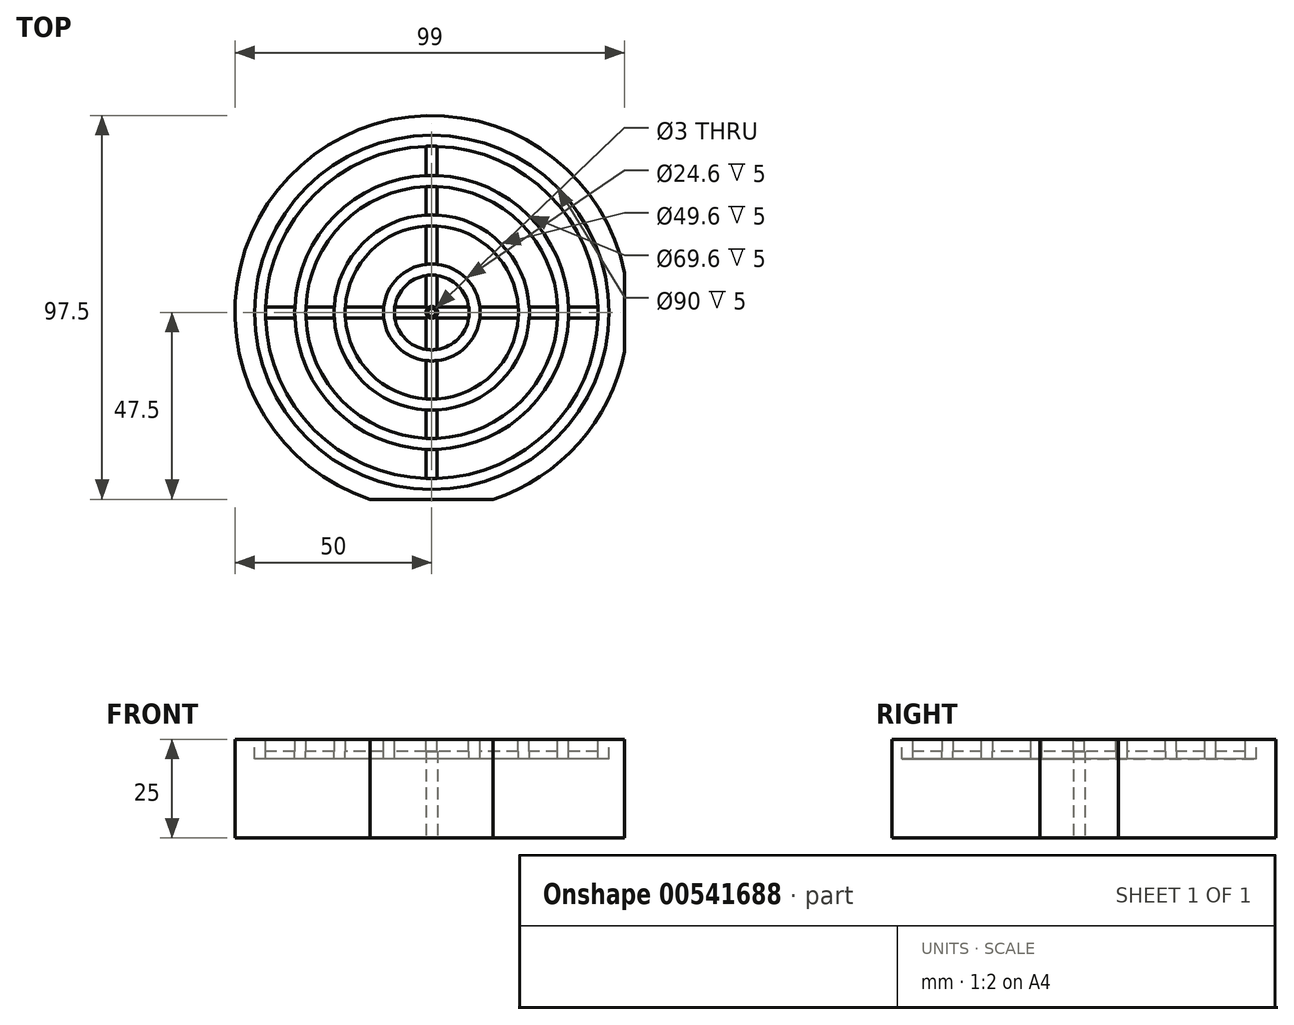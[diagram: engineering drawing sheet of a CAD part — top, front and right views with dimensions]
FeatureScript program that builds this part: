
annotation { "Feature Type Name" : "Feature", "Feature Type Description" : "" }
export const myFeature = defineFeature(function(context is Context, id is Id, definition is map)
    precondition{}
    {
        {
            var Q0;
            Q0=qCreatedBy(makeId("Top.planeOp"),FACE);
            var sketch = newSketch(context, id + "F0", { "sketchPlane" : qUnion([Q0])});
            skCircle(sketch, "E0", {"center": v(0, 0) * mm, "radius": 50 * mm});
            skCircle(sketch, "E1", {"center": v(0, 0) * mm, "radius": 1.5 * mm});
            skSolve(sketch);
        }
        {
            var Q0;
            Q0=qSketchRegion(id+"F0",true);
            extrude(context, id + "F1", {"entities" : qUnion([Q0]), "depth" : 25 * mm, "offsetDistance" : 25 * mm});
        }
        {
            var Q0;
            Q0=makeQuery(id+"F1.opExtrude","CAP_FACE",FACE,{"disambiguationData":[OSD([sQuery(id+"F0.wireOp",EDGE,"E0")])],"isStart":false});
            var sketch = newSketch(context, id + "F2", { "sketchPlane" : qUnion([Q0])});
            skCircle(sketch, "E2", {"center": v(0, 0) * mm, "radius": 45 * mm});
            skCircle(sketch, "E3.0", {"center": v(0, 0) * mm, "radius": 42.22 * mm});
            skCircle(sketch, "E4", {"center": v(0, 0) * mm, "radius": 32.5 * mm});
            skCircle(sketch, "E5.0", {"center": v(0, 0) * mm, "radius": 29.72 * mm});
            skCircle(sketch, "E6", {"center": v(0, 0) * mm, "radius": 22.5 * mm});
            skCircle(sketch, "E7", {"center": v(0, 0) * mm, "radius": 10 * mm});
            skCircle(sketch, "E8.0", {"center": v(0, 0) * mm, "radius": 7.22 * mm});
            skCircle(sketch, "E9.0", {"center": v(0, 0) * mm, "radius": 19.72 * mm});
            skLineSegment(sketch, "E10", {"start": v(-1, 44.99) * mm, "end": v(-1, 7.15) * mm});
            skLineSegment(sketch, "E11", {"start": v(1.39, 44.98) * mm, "end": v(1.4, -7.08) * mm});
            skLineSegment(sketch, "E12", {"start": v(0, 7.22) * mm, "end": v(0, 45) * mm, "construction": true});
            skLineSegment(sketch, "E13.1.0", {"start": v(-32.32, 31.02) * mm, "end": v(-5.57, 4.27) * mm});
            skLineSegment(sketch, "E13.1.1", {"start": v(-30.63, 32.7) * mm, "end": v(6.19, -4.1) * mm});
            skLineSegment(sketch, "E13.2.0", {"start": v(-44.6, -1) * mm, "end": v(-6.76, -1) * mm});
            skLineSegment(sketch, "E13.2.1", {"start": v(-44.59, 1.39) * mm, "end": v(7.47, 1.4) * mm});
            skPoint(sketch, "E13.center", {"position": v(0.2, 0.2) * mm});
            skLineSegment(sketch, "E14.2.3.0", {"start": v(-30.63, -32.32) * mm, "end": v(-3.88, -5.57) * mm});
            skLineSegment(sketch, "E14.3.3.0", {"start": v(-32.32, -30.63) * mm, "end": v(4.5, 6.19) * mm});
            skLineSegment(sketch, "E15.2.4.0", {"start": v(1.4, -44.6) * mm, "end": v(1.39, -6.76) * mm});
            skLineSegment(sketch, "E15.3.4.0", {"start": v(-1, -44.59) * mm, "end": v(-1, 7.47) * mm});
            skLineSegment(sketch, "E15.2.5.0", {"start": v(32.71, -30.63) * mm, "end": v(5.96, -3.88) * mm});
            skLineSegment(sketch, "E15.3.5.0", {"start": v(31.02, -32.32) * mm, "end": v(-5.8, 4.5) * mm});
            skLineSegment(sketch, "E15.2.6.0", {"start": v(44.99, 1.4) * mm, "end": v(7.15, 1.4) * mm});
            skLineSegment(sketch, "E15.3.6.0", {"start": v(44.98, -1) * mm, "end": v(-7.08, -1) * mm});
            skLineSegment(sketch, "E15.2.7.0", {"start": v(31.02, 32.71) * mm, "end": v(4.27, 5.96) * mm});
            skLineSegment(sketch, "E15.3.7.0", {"start": v(32.7, 31.02) * mm, "end": v(-4.1, -5.8) * mm});
            skLineSegment(sketch, "E16", {"start": v(7.15, 1.4) * mm, "end": v(7.47, 1.4) * mm});
            skLineSegment(sketch, "E17", {"start": v(-7.08, -1) * mm, "end": v(-6.76, -1) * mm});
            skLineSegment(sketch, "E18", {"start": v(1.4, -6.76) * mm, "end": v(1.4, -7.08) * mm});
            skLineSegment(sketch, "E19", {"start": v(-1, 7.47) * mm, "end": v(-1, 7.15) * mm});
            skSolve(sketch);
        }
        {
            var Q0;
            Q0=qSketchRegion(id+"F2",true);
            extrude(context, id + "F3", {"entities" : qUnion([Q0]), "operationType" : NewBodyOperationType.REMOVE, "oppositeDirection" : true, "depth" : 5 * mm, "offsetDistance" : 25 * mm});
        }
        {
            var Q0;
            {var subQ0=sQuery(id+"F0.wireOp",EDGE,"E1");Q0=makeQuery(id+"F3.boolean.opBoolean","SPLIT",FACE,{"disambiguationData":[TD([makeQuery(id+"F1.opExtrude","SWEPT_FACE",FACE,{"disambiguationData":[OSD([subQ0])]})])],"derivedFrom":makeQuery(id+"F1.opExtrude","CAP_FACE",FACE,{"disambiguationData":[OSD([sQuery(id+"F0.wireOp",EDGE,"E0"),subQ0])],"isStart":false})});}
            var sketch = newSketch(context, id + "F4", { "sketchPlane" : qUnion([Q0])});
            skCircle(sketch, "E20", {"center": v(0, 0) * mm, "radius": 9.5 * mm});
            skCircle(sketch, "E21", {"center": v(0, 0) * mm, "radius": 12.3 * mm});
            skSolve(sketch);
        }
        {
            var Q0;
            Q0=makeQuery(id+"F4.imprint","IMPRINT",FACE,{"disambiguationData":[TD([[makeQuery(id+"F4.imprint","IMPRINT",EDGE,{"derivedFrom":sQuery(id+"F4.wireOp",EDGE,"E20")}),-1.0]])]});
            extrude(context, id + "F5", {"entities" : qUnion([Q0]), "operationType" : NewBodyOperationType.REMOVE, "oppositeDirection" : true, "depth" : 5 * mm, "offsetDistance" : 25 * mm});
        }
        {
            var Q0;
            {var subQ0=makeQuery(id+"F3.opExtrude","SWEPT_FACE",FACE,{"disambiguationData":[OSD([sQuery(id+"F2.wireOp",EDGE,"E3.0")])]});var subQ1=sQuery(id+"F0.wireOp",EDGE,"E1");Q0=makeQuery(id+"F5.boolean.opBoolean","SPLIT",FACE,{"disambiguationData":[TD([makeQuery(id+"F3.boolean.opBoolean","COPY",FACE,{"derivedFrom":subQ0})])],"derivedFrom":makeQuery(id+"F3.boolean.opBoolean","SPLIT",FACE,{"disambiguationData":[TD([makeQuery(id+"F1.opExtrude","SWEPT_FACE",FACE,{"disambiguationData":[OSD([subQ1])]})])],"derivedFrom":makeQuery(id+"F1.opExtrude","CAP_FACE",FACE,{"disambiguationData":[OSD([sQuery(id+"F0.wireOp",EDGE,"E0"),subQ1])],"isStart":false})})});}
            var sketch = newSketch(context, id + "F6", { "sketchPlane" : qUnion([Q0])});
            skCircle(sketch, "E22", {"center": v(0, 0) * mm, "radius": 22 * mm});
            skCircle(sketch, "E23", {"center": v(0, 0) * mm, "radius": 24.8 * mm});
            skSolve(sketch);
        }
        {
            var Q0;
            Q0=makeQuery(id+"F6.imprint","IMPRINT",FACE,{"disambiguationData":[TD([[makeQuery(id+"F6.imprint","IMPRINT",EDGE,{"derivedFrom":sQuery(id+"F6.wireOp",EDGE,"E22")}),-1.0]])]});
            extrude(context, id + "F7", {"entities" : qUnion([Q0]), "operationType" : NewBodyOperationType.REMOVE, "oppositeDirection" : true, "depth" : 5 * mm, "offsetDistance" : 25 * mm});
        }
        {
            var Q0;
            {var subQ0=makeQuery(id+"F3.opExtrude","SWEPT_FACE",FACE,{"disambiguationData":[OSD([sQuery(id+"F2.wireOp",EDGE,"E3.0")])]});var subQ1=makeQuery(id+"F3.boolean.opBoolean","COPY",FACE,{"derivedFrom":subQ0});var subQ2=sQuery(id+"F0.wireOp",EDGE,"E1");Q0=makeQuery(id+"F7.boolean.opBoolean","SPLIT",FACE,{"disambiguationData":[TD([subQ1])],"derivedFrom":makeQuery(id+"F5.boolean.opBoolean","SPLIT",FACE,{"disambiguationData":[TD([subQ1])],"derivedFrom":makeQuery(id+"F3.boolean.opBoolean","SPLIT",FACE,{"disambiguationData":[TD([makeQuery(id+"F1.opExtrude","SWEPT_FACE",FACE,{"disambiguationData":[OSD([subQ2])]})])],"derivedFrom":makeQuery(id+"F1.opExtrude","CAP_FACE",FACE,{"disambiguationData":[OSD([sQuery(id+"F0.wireOp",EDGE,"E0"),subQ2])],"isStart":false})})})});}
            var sketch = newSketch(context, id + "F8", { "sketchPlane" : qUnion([Q0])});
            skCircle(sketch, "E24", {"center": v(0, 0) * mm, "radius": 32 * mm});
            skCircle(sketch, "E25", {"center": v(0, 0) * mm, "radius": 34.8 * mm});
            skSolve(sketch);
        }
        {
            var Q0;
            Q0=makeQuery(id+"F8.imprint","IMPRINT",FACE,{"disambiguationData":[TD([[makeQuery(id+"F8.imprint","IMPRINT",EDGE,{"derivedFrom":sQuery(id+"F8.wireOp",EDGE,"E24")}),-1.0]])]});
            extrude(context, id + "F9", {"entities" : qUnion([Q0]), "operationType" : NewBodyOperationType.REMOVE, "oppositeDirection" : true, "depth" : 5 * mm, "offsetDistance" : 25 * mm});
        }
        {
            var Q0;
            {var subQ0=sQuery(id+"F0.wireOp",EDGE,"E0");Q0=makeQuery(id+"F3.boolean.opBoolean","SPLIT",FACE,{"disambiguationData":[TD([makeQuery(id+"F1.opExtrude","SWEPT_FACE",FACE,{"disambiguationData":[OSD([subQ0])]})])],"derivedFrom":makeQuery(id+"F1.opExtrude","CAP_FACE",FACE,{"disambiguationData":[OSD([subQ0,sQuery(id+"F0.wireOp",EDGE,"E1")])],"isStart":false})});}
            var sketch = newSketch(context, id + "F10", { "sketchPlane" : qUnion([Q0])});
            skLineSegment(sketch, "E26.bottom", {"start": v(1.4, 44) * mm, "end": v(-1.4, 44) * mm});
            skLineSegment(sketch, "E26.top", {"start": v(1.4, -44) * mm, "end": v(-1.4, -44) * mm});
            skLineSegment(sketch, "E26.left", {"start": v(1.4, 44) * mm, "end": v(1.4, -44) * mm});
            skLineSegment(sketch, "E26.right", {"start": v(-1.4, 44) * mm, "end": v(-1.4, -44) * mm});
            skPoint(sketch, "E26.middle", {"position": v(0, 0) * mm});
            skSolve(sketch);
        }
        {
            var Q0;
            Q0=makeQuery(id+"F10.imprint","IMPRINT",FACE,{"disambiguationData":[TD([[makeQuery(id+"F10.imprint","IMPRINT",EDGE,{"derivedFrom":makeQuery(id+"F1.opExtrude","CAP_EDGE",EDGE,{"disambiguationData":[OSD([sQuery(id+"F0.wireOp",EDGE,"E0")])],"isStart":false})}),1.0]])]});
            var sketch = newSketch(context, id + "F11", { "sketchPlane" : qUnion([Q0])});
            skLineSegment(sketch, "E27.bottom", {"start": v(44, -1.4) * mm, "end": v(-44, -1.4) * mm});
            skLineSegment(sketch, "E27.top", {"start": v(44, 1.4) * mm, "end": v(-44, 1.4) * mm});
            skLineSegment(sketch, "E27.left", {"start": v(44, -1.4) * mm, "end": v(44, 1.4) * mm});
            skLineSegment(sketch, "E27.right", {"start": v(-44, -1.4) * mm, "end": v(-44, 1.4) * mm});
            skPoint(sketch, "E27.middle", {"position": v(0, 0) * mm});
            skSolve(sketch);
        }
        {
            var Q0;
            Q0=qSketchRegion(id+"F10",true);
            var Q1;
            Q1=qSketchRegion(id+"F11",true);
            extrude(context, id + "F12", {"entities" : qUnion([Q0, Q1]), "operationType" : NewBodyOperationType.REMOVE, "oppositeDirection" : true, "depth" : 3 * mm, "offsetDistance" : 25 * mm});
        }
        {
            var Q0;
            {var subQ0=sQuery(id+"F0.wireOp",EDGE,"E0");Q0=makeQuery(id+"F3.boolean.opBoolean","SPLIT",FACE,{"disambiguationData":[TD([makeQuery(id+"F1.opExtrude","SWEPT_FACE",FACE,{"disambiguationData":[OSD([subQ0])]})])],"derivedFrom":makeQuery(id+"F1.opExtrude","CAP_FACE",FACE,{"disambiguationData":[OSD([subQ0,sQuery(id+"F0.wireOp",EDGE,"E1")])],"isStart":false})});}
            var sketch = newSketch(context, id + "F13", { "sketchPlane" : qUnion([Q0])});
            skLineSegment(sketch, "E28.bottom", {"start": v(18, -52.5) * mm, "end": v(-18, -52.5) * mm});
            skLineSegment(sketch, "E28.top", {"start": v(18, -47.5) * mm, "end": v(-18, -47.5) * mm});
            skLineSegment(sketch, "E28.left", {"start": v(18, -52.5) * mm, "end": v(18, -47.5) * mm});
            skLineSegment(sketch, "E28.right", {"start": v(-18, -52.5) * mm, "end": v(-18, -47.5) * mm});
            skPoint(sketch, "E28.middle", {"position": v(0, -50) * mm});
            skLineSegment(sketch, "E29.bottom", {"start": v(51, -14.5) * mm, "end": v(49, -14.5) * mm});
            skLineSegment(sketch, "E29.top", {"start": v(51, 14.5) * mm, "end": v(49, 14.5) * mm});
            skLineSegment(sketch, "E29.left", {"start": v(51, -14.5) * mm, "end": v(51, 14.5) * mm});
            skLineSegment(sketch, "E29.right", {"start": v(49, -14.5) * mm, "end": v(49, 14.5) * mm});
            skPoint(sketch, "E29.middle", {"position": v(50, 0) * mm});
            skSolve(sketch);
        }
        {
            var Q0;
            Q0=qSketchRegion(id+"F13",true);
            extrude(context, id + "F14", {"entities" : qUnion([Q0]), "operationType" : NewBodyOperationType.REMOVE, "oppositeDirection" : true, "depth" : 25 * mm, "offsetDistance" : 25 * mm});
        }
        {
            var Q0;
            {var subQ0=sQuery(id+"F0.wireOp",EDGE,"E0");Q0=makeQuery(id+"F3.boolean.opBoolean","SPLIT",FACE,{"disambiguationData":[TD([makeQuery(id+"F1.opExtrude","SWEPT_FACE",FACE,{"disambiguationData":[OSD([subQ0])]})])],"derivedFrom":makeQuery(id+"F1.opExtrude","CAP_FACE",FACE,{"disambiguationData":[OSD([subQ0,sQuery(id+"F0.wireOp",EDGE,"E1")])],"isStart":false})});}
            var sketch = newSketch(context, id + "F15", { "sketchPlane" : qUnion([Q0])});
            skCircle(sketch, "E30", {"center": v(0, 0) * mm, "radius": 1 * mm});
            skSolve(sketch);
        }
        {
            var Q0;
            Q0=qSketchRegion(id+"F15",true);
            extrude(context, id + "F16", {"entities" : qUnion([Q0]), "oppositeDirection" : true, "depth" : .25 * mm, "offsetDistance" : 25 * mm});
        }
    });
